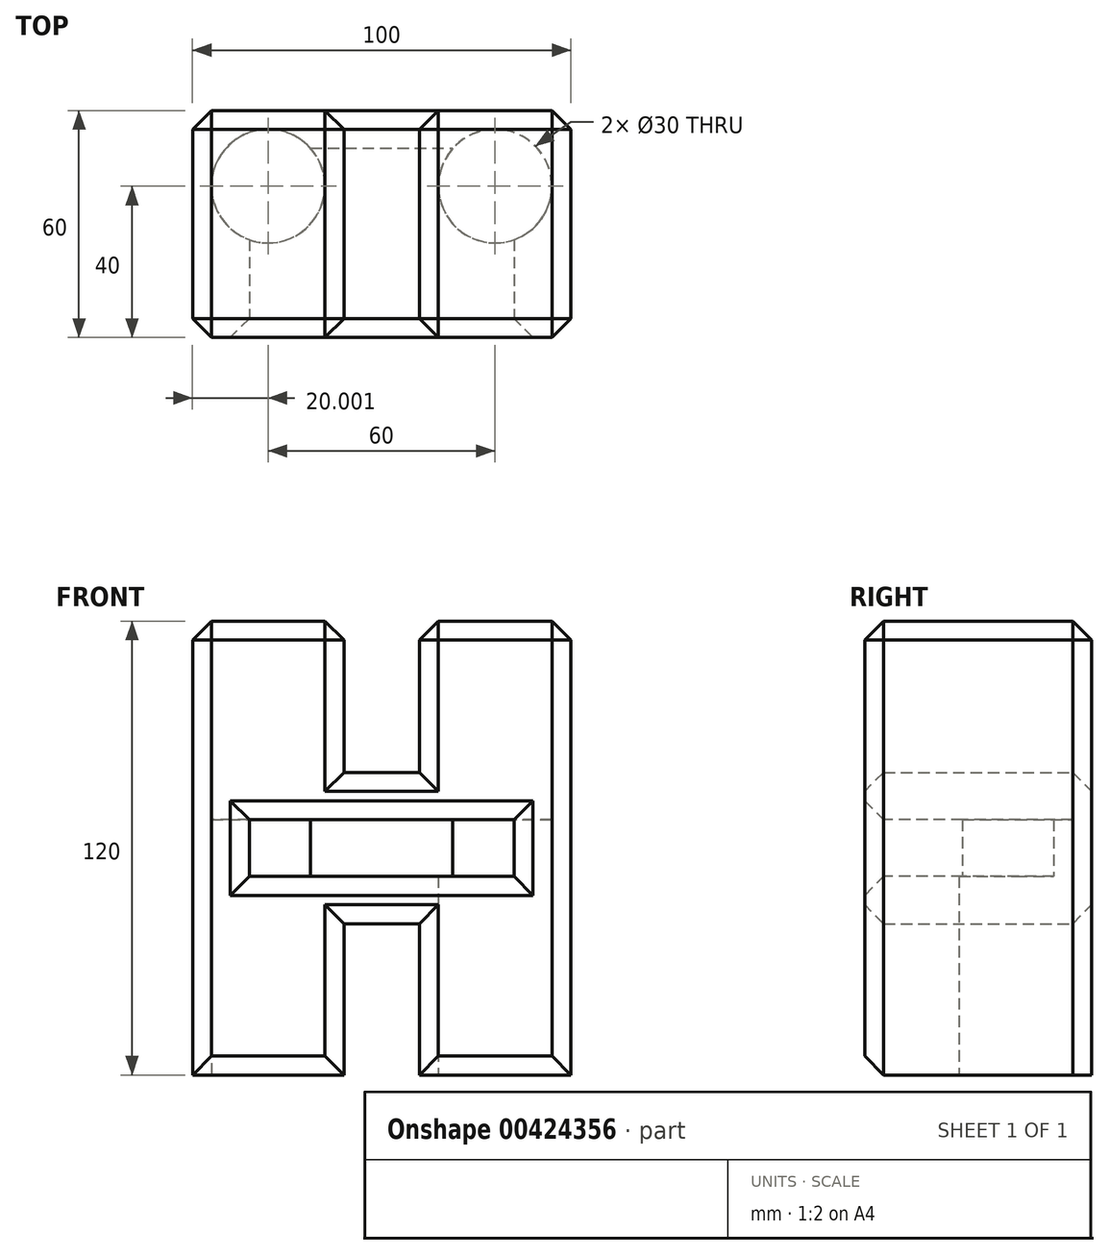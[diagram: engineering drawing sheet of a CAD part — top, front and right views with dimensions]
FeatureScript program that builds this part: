
annotation { "Feature Type Name" : "Feature", "Feature Type Description" : "" }
export const myFeature = defineFeature(function(context is Context, id is Id, definition is map)
    precondition{}
    {
        {
            var Q0;
            Q0=qCreatedBy(makeId("Front.planeOp"),FACE);
            var sketch = newSketch(context, id + "F0", { "sketchPlane" : qUnion([Q0])});
            skLineSegment(sketch, "E0.bottom", {"start": v(-48.04, 59.25) * mm, "end": v(-8.04, 59.25) * mm});
            skLineSegment(sketch, "E0.top", {"start": v(-48.04, -60.75) * mm, "end": v(-8.04, -60.75) * mm});
            skLineSegment(sketch, "E0.left", {"start": v(-48.04, 59.25) * mm, "end": v(-48.04, -60.75) * mm});
            skLineSegment(sketch, "E0.right", {"start": v(51.96, 59.25) * mm, "end": v(51.96, -60.75) * mm});
            skLineSegment(sketch, "E1", {"start": v(-8.04, 59.25) * mm, "end": v(-8.04, 19.25) * mm});
            skLineSegment(sketch, "E2", {"start": v(-8.04, 19.25) * mm, "end": v(11.96, 19.25) * mm});
            skLineSegment(sketch, "E3", {"start": v(11.96, 19.25) * mm, "end": v(11.96, 59.25) * mm});
            skLineSegment(sketch, "E4", {"start": v(11.96, -60.75) * mm, "end": v(11.96, -20.75) * mm});
            skLineSegment(sketch, "E5", {"start": v(11.96, -20.75) * mm, "end": v(-8.04, -20.75) * mm});
            skLineSegment(sketch, "E6", {"start": v(-8.04, -20.75) * mm, "end": v(-8.04, -60.75) * mm});
            skLineSegment(sketch, "E7.trimOffspring", {"start": v(11.96, -60.75) * mm, "end": v(51.96, -60.75) * mm});
            skLineSegment(sketch, "E8.trimOffspring", {"start": v(11.96, 59.25) * mm, "end": v(51.96, 59.25) * mm});
            skSolve(sketch);
        }
        {
            var Q0;
            Q0=makeQuery(id+"F0.imprint","IMPRINT",FACE,{"disambiguationData":[TD([[makeQuery(id+"F0.imprint","IMPRINT",EDGE,{"derivedFrom":sQuery(id+"F0.wireOp",EDGE,"E0.bottom")}),-1.0]])]});
            extrude(context, id + "F1", {"entities" : qUnion([Q0]), "depth" : 60 * mm});
        }
        {
            var Q0;
            Q0=makeQuery(id+"F1.opExtrude","CAP_FACE",FACE,{"disambiguationData":[OSD([sQuery(id+"F0.wireOp",EDGE,"E0.bottom"),sQuery(id+"F0.wireOp",EDGE,"E0.top"),sQuery(id+"F0.wireOp",EDGE,"E0.left"),sQuery(id+"F0.wireOp",EDGE,"E0.right"),sQuery(id+"F0.wireOp",EDGE,"E1"),sQuery(id+"F0.wireOp",EDGE,"E2"),sQuery(id+"F0.wireOp",EDGE,"E3"),sQuery(id+"F0.wireOp",EDGE,"E4"),sQuery(id+"F0.wireOp",EDGE,"E5"),sQuery(id+"F0.wireOp",EDGE,"E6"),sQuery(id+"F0.wireOp",EDGE,"E7.trimOffspring"),sQuery(id+"F0.wireOp",EDGE,"E8.trimOffspring")])],"isStart":false});
            var sketch = newSketch(context, id + "F2", { "sketchPlane" : qUnion([Q0])});
            skLineSegment(sketch, "E9.bottom", {"start": v(-33.04, 6.75) * mm, "end": v(36.96, 6.75) * mm});
            skLineSegment(sketch, "E9.top", {"start": v(-33.04, -8.25) * mm, "end": v(36.96, -8.25) * mm});
            skLineSegment(sketch, "E9.left", {"start": v(-33.04, 6.75) * mm, "end": v(-33.04, -8.25) * mm});
            skLineSegment(sketch, "E9.right", {"start": v(36.96, 6.75) * mm, "end": v(36.96, -8.25) * mm});
            skSolve(sketch);
        }
        {
            var Q0;
            Q0=makeQuery(id+"F2.imprint","IMPRINT",FACE,{"disambiguationData":[TD([[makeQuery(id+"F2.imprint","IMPRINT",EDGE,{"derivedFrom":sQuery(id+"F2.wireOp",EDGE,"E9.bottom")}),-1.0]])]});
            extrude(context, id + "F3", {"entities" : qUnion([Q0]), "operationType" : NewBodyOperationType.REMOVE, "oppositeDirection" : true, "depth" : 50 * mm});
        }
        {
            var Q0;
            Q0=makeQuery(id+"F1.opExtrude","SWEPT_FACE",FACE,{"disambiguationData":[OSD([sQuery(id+"F0.wireOp",EDGE,"E0.top")])]});
            var sketch = newSketch(context, id + "F4", { "sketchPlane" : qUnion([Q0])});
            skCircle(sketch, "E10", {"center": v(-28.04, 20) * mm, "radius": 15 * mm});
            skSolve(sketch);
        }
        {
            var Q0;
            Q0=makeQuery(id+"F1.opExtrude","SWEPT_FACE",FACE,{"disambiguationData":[OSD([sQuery(id+"F0.wireOp",EDGE,"E7.trimOffspring")])]});
            var sketch = newSketch(context, id + "F5", { "sketchPlane" : qUnion([Q0])});
            skCircle(sketch, "E11", {"center": v(31.96, 20) * mm, "radius": 15 * mm});
            skSolve(sketch);
        }
        {
            var Q0;
            Q0=makeQuery(id+"F4.imprint","IMPRINT",FACE,{"disambiguationData":[TD([[makeQuery(id+"F4.imprint","IMPRINT",EDGE,{"derivedFrom":sQuery(id+"F4.wireOp",EDGE,"E10")}),1.0]])]});
            var Q1;
            Q1=makeQuery(id+"F5.imprint","IMPRINT",FACE,{"disambiguationData":[TD([[makeQuery(id+"F5.imprint","IMPRINT",EDGE,{"derivedFrom":sQuery(id+"F5.wireOp",EDGE,"E11")}),1.0]])]});
            var Q2;
            Q2=sQuery(id+"F4.wireOp",EDGE,"E10");
            extrude(context, id + "F6", {"entities" : qUnion([Q0, Q1]), "operationType" : NewBodyOperationType.REMOVE, "surfaceEntities" : qUnion([Q2]), "oppositeDirection" : true, "depth" : 67.5 * mm});
        }
        {
            var Q0;
            Q0=makeQuery(id+"F1.opExtrude","SWEPT_EDGE",EDGE,{"disambiguationData":[OSD([sQuery(id+"F0.wireOp",EDGE,"E0.bottom"),sQuery(id+"F0.wireOp",EDGE,"E0.left")])]});
            var Q1;
            Q1=makeQuery(id+"F1.opExtrude","SWEPT_EDGE",EDGE,{"disambiguationData":[OSD([sQuery(id+"F0.wireOp",EDGE,"E0.bottom"),sQuery(id+"F0.wireOp",EDGE,"E1")])]});
            var Q2;
            Q2=makeQuery(id+"F1.opExtrude","SWEPT_EDGE",EDGE,{"disambiguationData":[OSD([sQuery(id+"F0.wireOp",EDGE,"E3"),sQuery(id+"F0.wireOp",EDGE,"E8.trimOffspring")])]});
            var Q3;
            Q3=makeQuery(id+"F1.opExtrude","SWEPT_EDGE",EDGE,{"disambiguationData":[OSD([sQuery(id+"F0.wireOp",EDGE,"E0.right"),sQuery(id+"F0.wireOp",EDGE,"E8.trimOffspring")])]});
            var Q4;
            Q4=makeQuery(id+"F1.opExtrude","CAP_EDGE",EDGE,{"disambiguationData":[OSD([sQuery(id+"F0.wireOp",EDGE,"E8.trimOffspring")])],"isStart":false});
            var Q5;
            Q5=makeQuery(id+"F1.opExtrude","CAP_EDGE",EDGE,{"disambiguationData":[OSD([sQuery(id+"F0.wireOp",EDGE,"E0.bottom")])],"isStart":false});
            var Q6;
            Q6=makeQuery(id+"F1.opExtrude","CAP_EDGE",EDGE,{"disambiguationData":[OSD([sQuery(id+"F0.wireOp",EDGE,"E8.trimOffspring")])],"isStart":true});
            var Q7;
            Q7=makeQuery(id+"F1.opExtrude","CAP_EDGE",EDGE,{"disambiguationData":[OSD([sQuery(id+"F0.wireOp",EDGE,"E0.bottom")])],"isStart":true});
            var Q8;
            Q8=makeQuery(id+"F3.boolean.opBoolean","COPY",EDGE,{"derivedFrom":makeQuery(id+"F3.opExtrude","CAP_EDGE",EDGE,{"disambiguationData":[OSD([sQuery(id+"F2.wireOp",EDGE,"E9.bottom")])],"isStart":true})});
            var Q9;
            Q9=makeQuery(id+"F3.boolean.opBoolean","COPY",EDGE,{"derivedFrom":makeQuery(id+"F3.opExtrude","CAP_EDGE",EDGE,{"disambiguationData":[OSD([sQuery(id+"F2.wireOp",EDGE,"E9.left")])],"isStart":true})});
            var Q10;
            Q10=makeQuery(id+"F3.boolean.opBoolean","COPY",EDGE,{"derivedFrom":makeQuery(id+"F3.opExtrude","CAP_EDGE",EDGE,{"disambiguationData":[OSD([sQuery(id+"F2.wireOp",EDGE,"E9.top")])],"isStart":true})});
            var Q11;
            Q11=makeQuery(id+"F3.boolean.opBoolean","COPY",EDGE,{"derivedFrom":makeQuery(id+"F3.opExtrude","CAP_EDGE",EDGE,{"disambiguationData":[OSD([sQuery(id+"F2.wireOp",EDGE,"E9.right")])],"isStart":true})});
            var Q12;
            Q12=makeQuery(id+"F1.opExtrude","CAP_EDGE",EDGE,{"disambiguationData":[OSD([sQuery(id+"F0.wireOp",EDGE,"E0.right")])],"isStart":false});
            var Q13;
            Q13=makeQuery(id+"F1.opExtrude","CAP_EDGE",EDGE,{"disambiguationData":[OSD([sQuery(id+"F0.wireOp",EDGE,"E0.right")])],"isStart":true});
            var Q14;
            Q14=makeQuery(id+"F1.opExtrude","CAP_FACE",FACE,{"disambiguationData":[OSD([sQuery(id+"F0.wireOp",EDGE,"E0.bottom"),sQuery(id+"F0.wireOp",EDGE,"E0.top"),sQuery(id+"F0.wireOp",EDGE,"E0.left"),sQuery(id+"F0.wireOp",EDGE,"E0.right"),sQuery(id+"F0.wireOp",EDGE,"E1"),sQuery(id+"F0.wireOp",EDGE,"E2"),sQuery(id+"F0.wireOp",EDGE,"E3"),sQuery(id+"F0.wireOp",EDGE,"E4"),sQuery(id+"F0.wireOp",EDGE,"E5"),sQuery(id+"F0.wireOp",EDGE,"E6"),sQuery(id+"F0.wireOp",EDGE,"E7.trimOffspring"),sQuery(id+"F0.wireOp",EDGE,"E8.trimOffspring")])],"isStart":false});
            var Q15;
            Q15=makeQuery(id+"F1.opExtrude","CAP_EDGE",EDGE,{"disambiguationData":[OSD([sQuery(id+"F0.wireOp",EDGE,"E0.left")])],"isStart":true});
            var Q16;
            Q16=makeQuery(id+"F1.opExtrude","CAP_EDGE",EDGE,{"disambiguationData":[OSD([sQuery(id+"F0.wireOp",EDGE,"E4")])],"isStart":true});
            var Q17;
            Q17=makeQuery(id+"F1.opExtrude","CAP_EDGE",EDGE,{"disambiguationData":[OSD([sQuery(id+"F0.wireOp",EDGE,"E6")])],"isStart":true});
            var Q18;
            Q18=makeQuery(id+"F1.opExtrude","CAP_EDGE",EDGE,{"disambiguationData":[OSD([sQuery(id+"F0.wireOp",EDGE,"E3")])],"isStart":true});
            var Q19;
            Q19=makeQuery(id+"F1.opExtrude","CAP_EDGE",EDGE,{"disambiguationData":[OSD([sQuery(id+"F0.wireOp",EDGE,"E1")])],"isStart":true});
            chamfer(context, id + "F7", {"entities" : qUnion([Q0, Q1, Q2, Q3, Q4, Q5, Q6, Q7, Q8, Q9, Q10, Q11, Q12, Q13, Q14, Q15, Q16, Q17, Q18, Q19]), "width" : 5 * mm, "tangentPropagation" : true});
        }
        {
            var Q0;
            Q0=makeQuery(id+"F1.opExtrude","CAP_EDGE",EDGE,{"disambiguationData":[OSD([sQuery(id+"F0.wireOp",EDGE,"E5")])],"isStart":true});
            chamfer(context, id + "F8", {"entities" : qUnion([Q0]), "width" : 5 * mm, "tangentPropagation" : true});
        }
        {
            var Q0;
            Q0=makeQuery(id+"F1.opExtrude","CAP_EDGE",EDGE,{"disambiguationData":[OSD([sQuery(id+"F0.wireOp",EDGE,"E2")])],"isStart":true});
            chamfer(context, id + "F9", {"entities" : qUnion([Q0]), "width" : 5 * mm, "tangentPropagation" : true});
        }
    });
